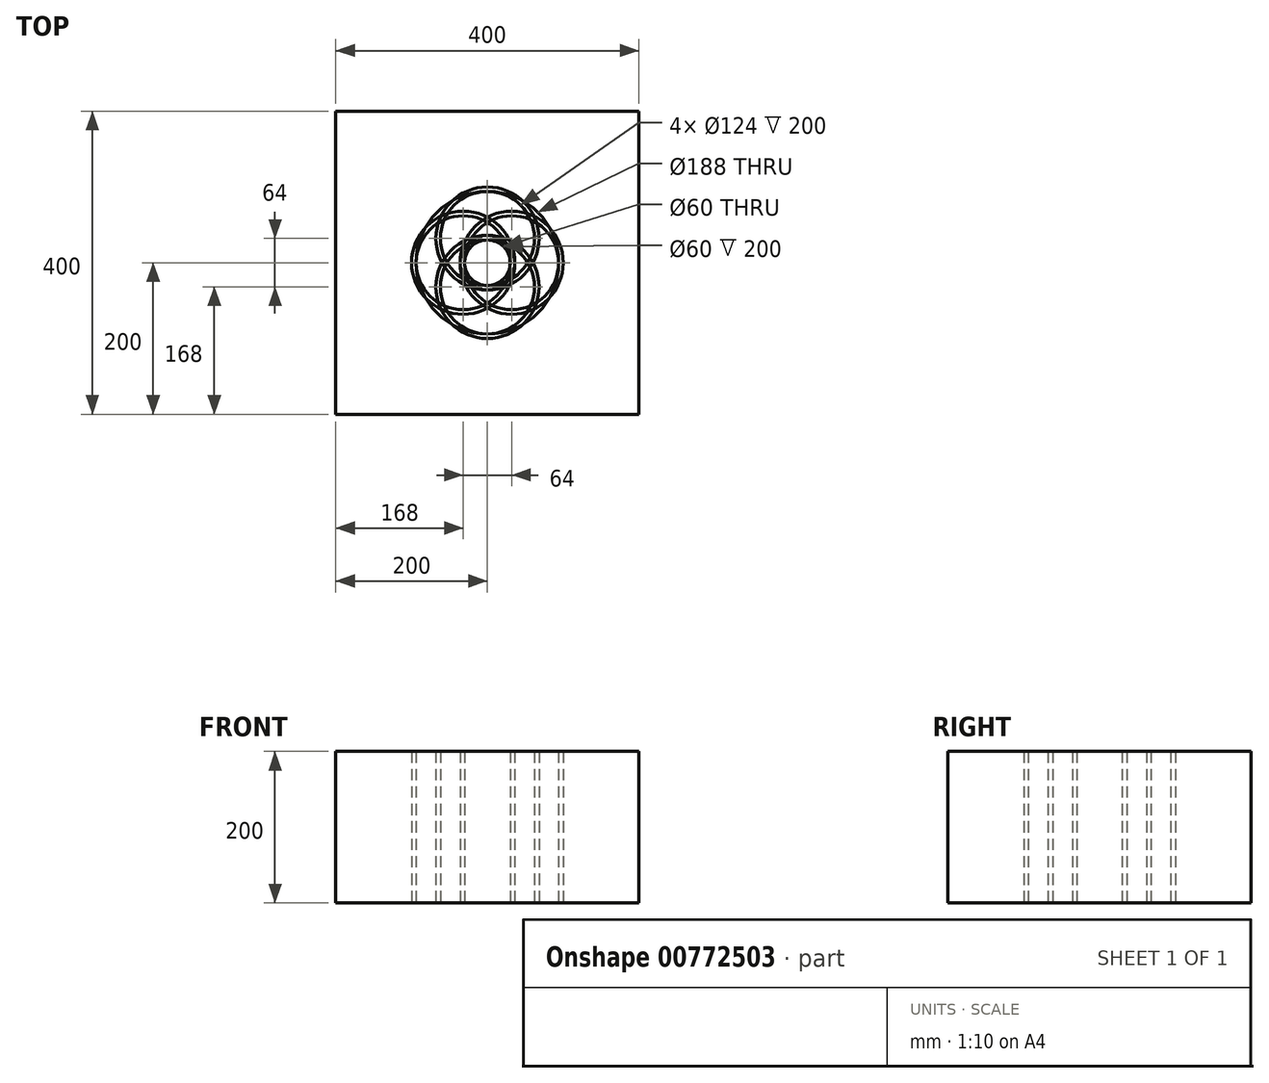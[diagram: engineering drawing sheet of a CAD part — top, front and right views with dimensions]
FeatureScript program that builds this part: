
annotation { "Feature Type Name" : "Feature", "Feature Type Description" : "" }
export const myFeature = defineFeature(function(context is Context, id is Id, definition is map)
    precondition{}
    {
        {
            assignVariable(context, id + "F0", {"name" : "Outer_Radius", "anyValue" : 100});
        }
        {
            assignVariable(context, id + "F1", {"name" : "Spoke_Count", "anyValue" : 4});
        }
        {
            var Q0;
            Q0=qCreatedBy(makeId("Top.planeOp"),FACE);
            var sketch = newSketch(context, id + "F2", { "sketchPlane" : qUnion([Q0])});
            skLineSegment(sketch, "E0.bottom", {"start": v(200, -200) * mm, "end": v(-200, -200) * mm});
            skLineSegment(sketch, "E0.top", {"start": v(200, 200) * mm, "end": v(-200, 200) * mm});
            skLineSegment(sketch, "E0.left", {"start": v(200, -200) * mm, "end": v(200, 200) * mm});
            skLineSegment(sketch, "E0.right", {"start": v(-200, -200) * mm, "end": v(-200, 200) * mm});
            skPoint(sketch, "E0.middle", {"position": v(0, 0) * mm});
            skCircle(sketch, "E1", {"center": v(0, 0) * mm, "radius": 30 * mm});
            skSolve(sketch);
        }
        {
            var Q0;
            Q0 = qSketchRegion(id + "F2", true);
            extrude(context, id + "F3", {"entities" : qUnion([Q0]), "endBound" : BoundingType.SYMMETRIC, "depth" : (2 * getVariable(context, 'Outer_Radius')) * mm, "offsetDistance" : 25 * mm});
        }
        {
            var Q0;
            Q0=qCreatedBy(makeId("Front.planeOp"),FACE);
            var sketch = newSketch(context, id + "F4", { "sketchPlane" : qUnion([Q0])});
            skLineSegment(sketch, "E2", {"start": v(0, -68.24) * mm, "end": v(0, 69.92) * mm, "construction": true});
            skSolve(sketch);
        }
        {
            var Q0;
            Q0=qCreatedBy(makeId("Top.planeOp"),FACE);
            var sketch = newSketch(context, id + "F5", { "sketchPlane" : qUnion([Q0])});
            skCircle(sketch, "E3", {"center": v(0, 0) * mm, "radius": 36 * mm});
            skCircle(sketch, "E4", {"center": v(0, 0) * mm, "radius": 94 * mm});
            skLineSegment(sketch, "E5.bottom", {"start": v(200, -200) * mm, "end": v(-200, -200) * mm});
            skLineSegment(sketch, "E5.top", {"start": v(200, 200) * mm, "end": v(-200, 200) * mm});
            skLineSegment(sketch, "E5.left", {"start": v(200, -200) * mm, "end": v(200, 200) * mm});
            skLineSegment(sketch, "E5.right", {"start": v(-200, -200) * mm, "end": v(-200, 200) * mm});
            skCircle(sketch, "E6", {"center": v(0, 0) * mm, "radius": 30 * mm});
            skSolve(sketch);
        }
        {
            var Q0;
            Q0=qCreatedBy(makeId("Top.planeOp"),FACE);
            var sketch = newSketch(context, id + "F6", { "sketchPlane" : qUnion([Q0])});
            skLineSegment(sketch, "E7", {"start": v(0, -36) * mm, "end": v(0, 100) * mm, "construction": true});
            skPoint(sketch, "E8", {"position": v(0, 94) * mm});
            skCircle(sketch, "E9", {"center": v(0, 32) * mm, "radius": 68 * mm});
            skCircle(sketch, "E10", {"center": v(0, 32) * mm, "radius": 62 * mm});
            skSolve(sketch);
        }
        {
            var Q0;
            Q0 = qSketchRegion(id + "F6", true);
            extrude(context, id + "F7", {"entities" : qUnion([Q0]), "endBound" : BoundingType.SYMMETRIC, "depth" : (2 * getVariable(context, 'Outer_Radius')) * mm, "offsetDistance" : 25 * mm});
        }
        {
            var Q0;
            Q0=makeQuery(id+"F7.opExtrude","SWEPT_BODY",BODY,{"disambiguationData":[OSD([sQuery(id+"F6.wireOp",EDGE,"E9"),sQuery(id+"F6.wireOp",EDGE,"E10")])]});
            var Q1;
            Q1=sQuery(id+"F4.wireOp",EDGE,"E2");
            circularPattern(context, id + "F8", {"entities" : qUnion([Q0]), "axis" : qUnion([Q1]), "angle" : 360 * degree, "instanceCount" : getVariable(context, 'Spoke_Count'), "equalSpace" : true});
        }
        {
            var Q0;
            Q0 = qSketchRegion(id + "F5", true);
            var Q1;
            Q1=makeQuery(id+"F5.imprint","IMPRINT",FACE,{"disambiguationData":[TD([[makeQuery(id+"F5.imprint","IMPRINT",EDGE,{"derivedFrom":sQuery(id+"F5.wireOp",EDGE,"E3")}),1.0]])]});
            extrude(context, id + "F9", {"entities" : qUnion([Q0, Q1]), "endBound" : BoundingType.SYMMETRIC, "depth" : (2 * getVariable(context, 'Outer_Radius')) * mm, "offsetDistance" : 25 * mm});
        }
    });
